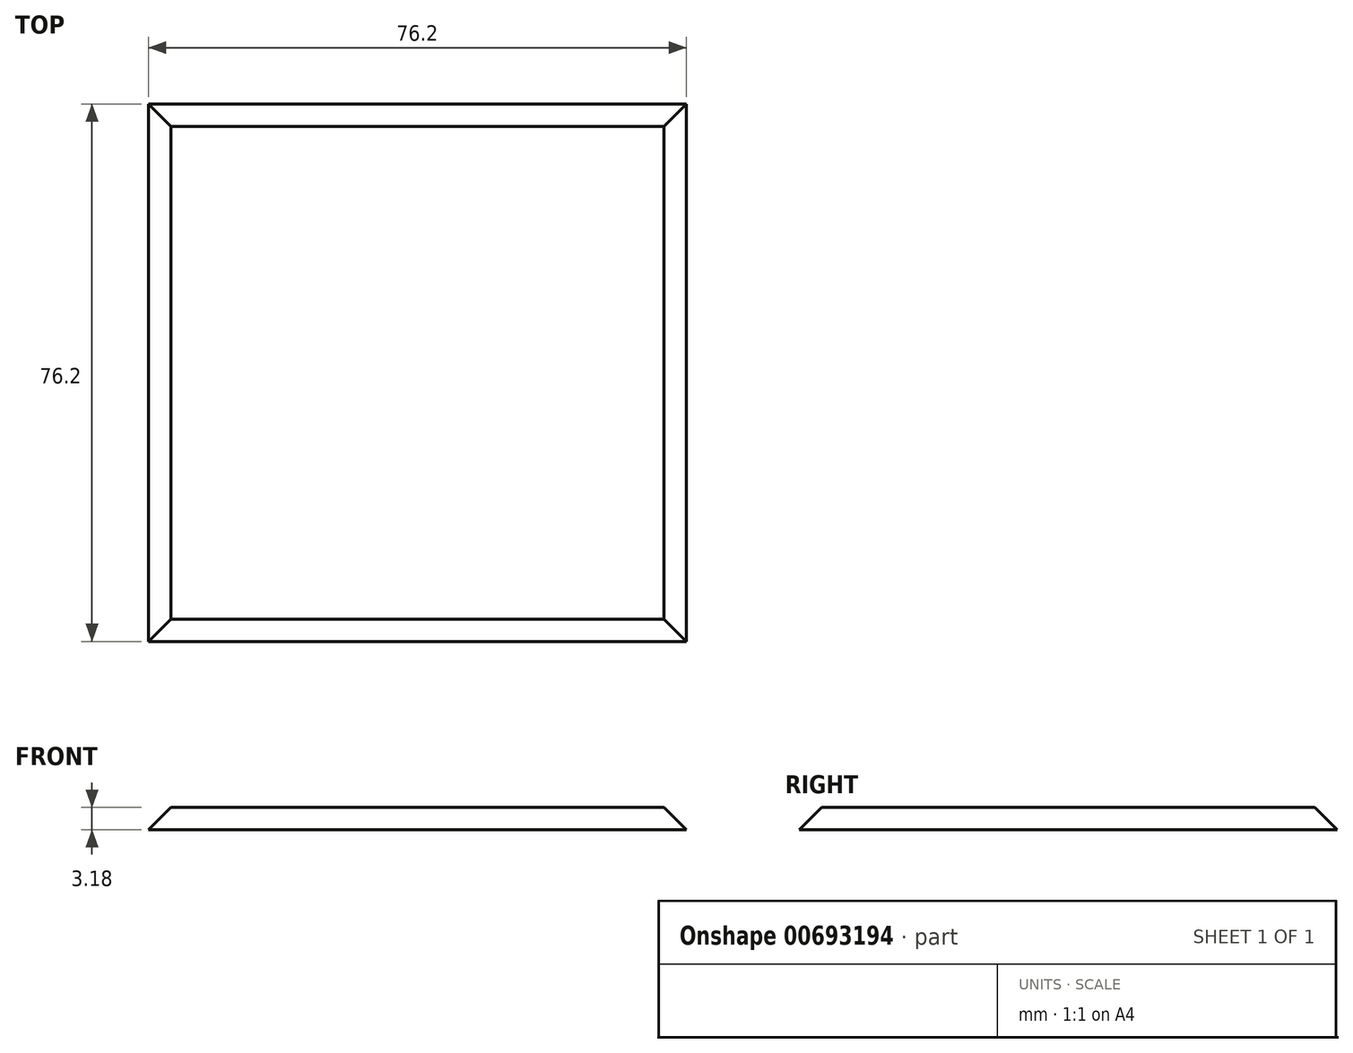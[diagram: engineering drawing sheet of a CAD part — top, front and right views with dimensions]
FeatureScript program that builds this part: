
annotation { "Feature Type Name" : "Feature", "Feature Type Description" : "" }
export const myFeature = defineFeature(function(context is Context, id is Id, definition is map)
    precondition{}
    {
        {
            var Q0;
            Q0=qCreatedBy(makeId("Top.planeOp"),FACE);
            var sketch = newSketch(context, id + "F0", { "sketchPlane" : qUnion([Q0])});
            skLineSegment(sketch, "E0.bottom", {"start": v(38.1, 38.1) * mm, "end": v(-38.1, 38.1) * mm});
            skLineSegment(sketch, "E0.top", {"start": v(38.1, -38.1) * mm, "end": v(-38.1, -38.1) * mm});
            skLineSegment(sketch, "E0.left", {"start": v(38.1, 38.1) * mm, "end": v(38.1, -38.1) * mm});
            skLineSegment(sketch, "E0.right", {"start": v(-38.1, 38.1) * mm, "end": v(-38.1, -38.1) * mm});
            skPoint(sketch, "E0.middle", {"position": v(0, 0) * mm});
            skSolve(sketch);
        }
        {
            var Q0;
            Q0=qSketchRegion(id+"F0",true);
            extrude(context, id + "F1", {"entities" : qUnion([Q0]), "depth" : 3.17 * mm, "offsetDistance" : 25.4 * mm});
        }
        {
            var Q0;
            Q0=makeQuery(id+"F1.opExtrude","SWEPT_FACE",FACE,{"disambiguationData":[OSD([sQuery(id+"F0.wireOp",EDGE,"E0.left")])]});
            var sketch = newSketch(context, id + "F2", { "sketchPlane" : qUnion([Q0])});
            skLineSegment(sketch, "E1", {"start": v(-38.1, 0) * mm, "end": v(-34.93, 3.17) * mm});
            skLineSegment(sketch, "E2", {"start": v(-34.93, 3.17) * mm, "end": v(-38.1, 3.18) * mm});
            skLineSegment(sketch, "E3", {"start": v(-38.1, 3.18) * mm, "end": v(-38.1, 0) * mm});
            skLineSegment(sketch, "E4", {"start": v(0, 12.24) * mm, "end": v(0, -11.06) * mm, "construction": true});
            skLineSegment(sketch, "E5.MirrorCS", {"start": v(38.1, 0) * mm, "end": v(34.93, 3.17) * mm});
            skLineSegment(sketch, "E6.MirrorCS", {"start": v(34.93, 3.17) * mm, "end": v(38.1, 3.18) * mm});
            skLineSegment(sketch, "E7.MirrorCS", {"start": v(38.1, 3.18) * mm, "end": v(38.1, 0) * mm});
            skSolve(sketch);
        }
        {
            var Q0;
            Q0=makeQuery(id+"F1.opExtrude","SWEPT_FACE",FACE,{"disambiguationData":[OSD([sQuery(id+"F0.wireOp",EDGE,"E0.bottom")])]});
            var sketch = newSketch(context, id + "F3", { "sketchPlane" : qUnion([Q0])});
            skLineSegment(sketch, "E8", {"start": v(-38.1, 0) * mm, "end": v(-34.93, 3.17) * mm});
            skLineSegment(sketch, "E9", {"start": v(-34.93, 3.18) * mm, "end": v(-38.1, 3.18) * mm});
            skLineSegment(sketch, "E10", {"start": v(-38.1, 3.18) * mm, "end": v(-38.1, 0) * mm});
            skLineSegment(sketch, "E11", {"start": v(0, 8.91) * mm, "end": v(0, -4.58) * mm, "construction": true});
            skLineSegment(sketch, "E12.MirrorCS", {"start": v(38.1, 0) * mm, "end": v(34.93, 3.17) * mm});
            skLineSegment(sketch, "E13.MirrorCS", {"start": v(34.93, 3.18) * mm, "end": v(38.1, 3.18) * mm});
            skLineSegment(sketch, "E14.MirrorCS", {"start": v(38.1, 3.18) * mm, "end": v(38.1, 0) * mm});
            skSolve(sketch);
        }
        {
            var Q0;
            Q0=makeQuery(id+"F3.imprint","IMPRINT",FACE,{"disambiguationData":[TD([[makeQuery(id+"F3.imprint","IMPRINT",EDGE,{"derivedFrom":sQuery(id+"F3.wireOp",EDGE,"E8")}),1.0]])]});
            var Q1;
            Q1=makeQuery(id+"F3.imprint","IMPRINT",FACE,{"disambiguationData":[TD([[makeQuery(id+"F3.imprint","IMPRINT",EDGE,{"derivedFrom":sQuery(id+"F3.wireOp",EDGE,"E12.MirrorCS")}),-1.0]])]});
            extrude(context, id + "F4", {"entities" : qUnion([Q0, Q1]), "operationType" : NewBodyOperationType.REMOVE, "oppositeDirection" : true, "depth" : 76.2 * mm, "offsetDistance" : 25.4 * mm});
        }
        {
            var Q0;
            Q0=makeQuery(id+"F2.imprint","IMPRINT",FACE,{"disambiguationData":[TD([[makeQuery(id+"F2.imprint","IMPRINT",EDGE,{"derivedFrom":sQuery(id+"F2.wireOp",EDGE,"E5.MirrorCS")}),-1.0]])]});
            var Q1;
            Q1=makeQuery(id+"F2.imprint","IMPRINT",FACE,{"disambiguationData":[TD([[makeQuery(id+"F2.imprint","IMPRINT",EDGE,{"derivedFrom":sQuery(id+"F2.wireOp",EDGE,"E1")}),1.0]])]});
            extrude(context, id + "F5", {"entities" : qUnion([Q0, Q1]), "operationType" : NewBodyOperationType.REMOVE, "oppositeDirection" : true, "depth" : 76.2 * mm, "offsetDistance" : 25.4 * mm});
        }
    });
